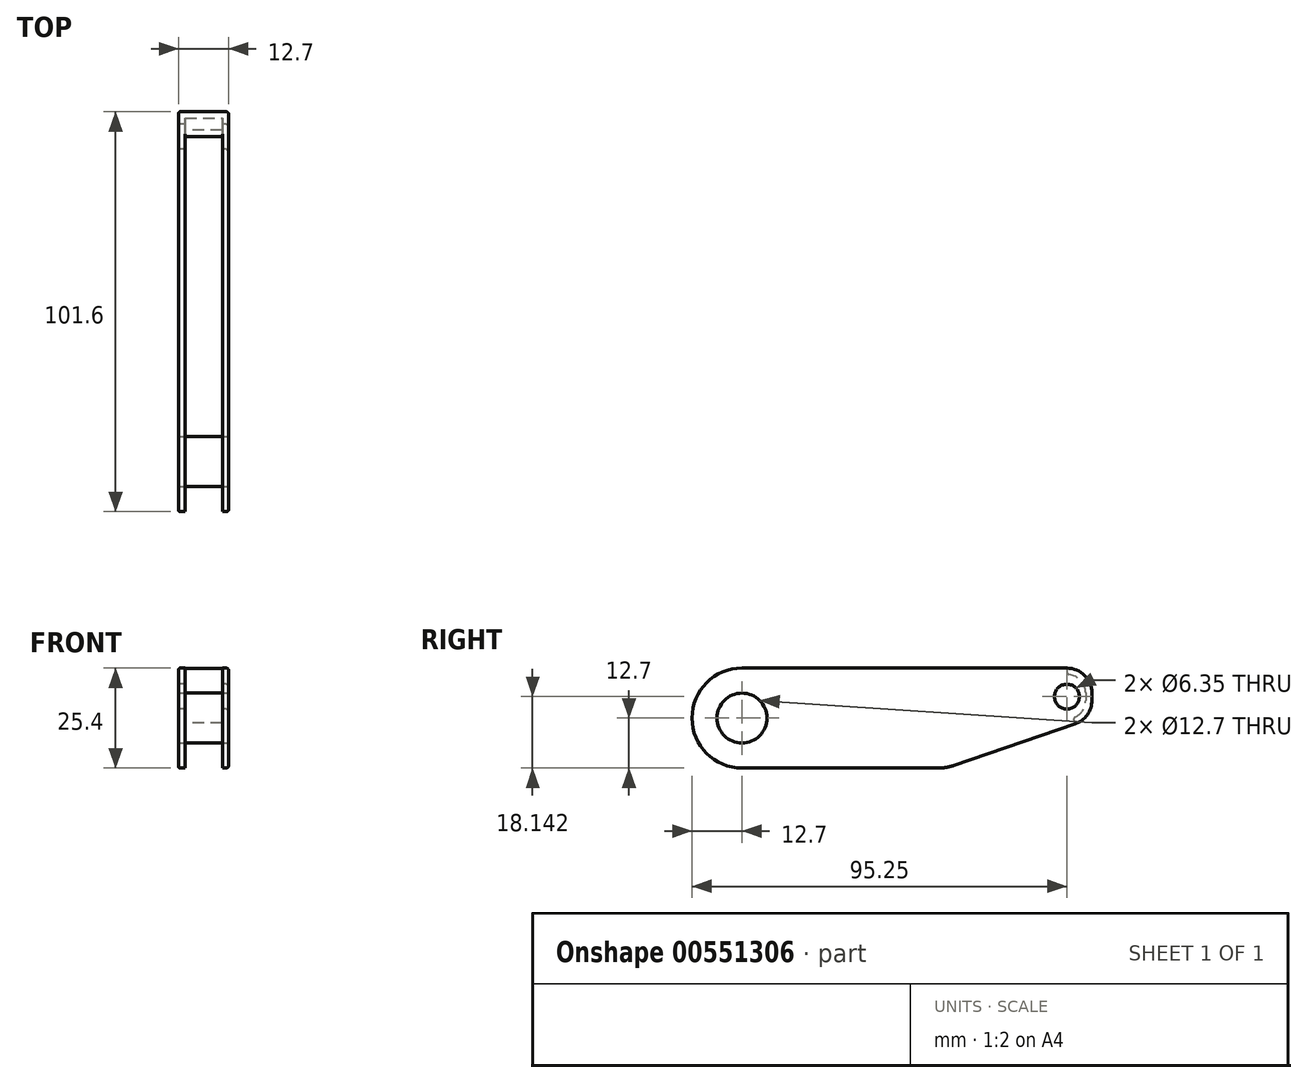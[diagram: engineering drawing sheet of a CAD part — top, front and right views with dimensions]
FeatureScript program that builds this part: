
annotation { "Feature Type Name" : "Feature", "Feature Type Description" : "" }
export const myFeature = defineFeature(function(context is Context, id is Id, definition is map)
    precondition{}
    {
        {
            var Q0;
            Q0=qCreatedBy(makeId("Right.planeOp"),FACE);
            var sketch = newSketch(context, id + "F0", { "sketchPlane" : qUnion([Q0])});
            skLineSegment(sketch, "E0.right", {"start": v(-50.8, 0) * mm, "end": v(-50.8, 0) * mm});
            skPoint(sketch, "E0.middle", {"position": v(0, 0) * mm});
            skArc(sketch, "E1.filletArc", {"start": v(-50.8, 0) * mm, "mid": v(-47.08, -8.98) * mm, "end": v(-38.1, -12.7) * mm});
            skArc(sketch, "E2.filletArc", {"start": v(-38.1, 12.7) * mm, "mid": v(-47.08, 8.98) * mm, "end": v(-50.8, 0) * mm});
            skLineSegment(sketch, "E3.MirrorCS", {"start": v(11.67, -12.7) * mm, "end": v(-38.1, -12.7) * mm});
            skArc(sketch, "E4.MirrorCS", {"start": v(15.8, -12.01) * mm, "mid": v(13.76, -12.53) * mm, "end": v(11.67, -12.7) * mm});
            skLineSegment(sketch, "E5.MirrorCS", {"start": v(15.8, -12.01) * mm, "end": v(46.51, -1.47) * mm});
            skArc(sketch, "E6.MirrorCS", {"start": v(50.8, 4.53) * mm, "mid": v(49.62, 0.84) * mm, "end": v(46.51, -1.47) * mm});
            skLineSegment(sketch, "E7.MirrorCS", {"start": v(50.8, 6.35) * mm, "end": v(50.8, 4.53) * mm});
            skArc(sketch, "E8.MirrorCS", {"start": v(44.45, 12.7) * mm, "mid": v(48.94, 10.84) * mm, "end": v(50.8, 6.35) * mm});
            skLineSegment(sketch, "E9", {"start": v(-38.1, 12.7) * mm, "end": v(44.45, 12.7) * mm});
            skPoint(sketch, "E10", {"position": v(-50.8, 0) * mm});
            skLineSegment(sketch, "E11", {"start": v(-38.1, 12.7) * mm, "end": v(-38.1, -12.7) * mm, "construction": true});
            skLineSegment(sketch, "E12", {"start": v(-38.1, 0) * mm, "end": v(-50.8, 0) * mm, "construction": true});
            skSolve(sketch);
        }
        {
            var Q0;
            Q0=makeQuery(id+"F0.imprint","IMPRINT",FACE,{"disambiguationData":[TD([[makeQuery(id+"F0.imprint","IMPRINT",EDGE,{"derivedFrom":sQuery(id+"F0.wireOp",EDGE,"E1.filletArc")}),1.0]])]});
            extrude(context, id + "F1", {"entities" : qUnion([Q0]), "depth" : 12.7 * mm, "offsetDistance" : 25.4 * mm, "symmetric" : true});
        }
        {
            var Q0;
            Q0=makeQuery(id+"F1.opExtrude","SWEPT_FACE",FACE,{"disambiguationData":[OSD([sQuery(id+"F0.wireOp",EDGE,"E1.filletArc"),sQuery(id+"F0.wireOp",EDGE,"E2.filletArc")])]});
            var Q1;
            Q1=makeQuery(id+"F1.opExtrude","SWEPT_FACE",FACE,{"disambiguationData":[OSD([sQuery(id+"F0.wireOp",EDGE,"E9")])]});
            var Q2;
            Q2=makeQuery(id+"F1.opExtrude","SWEPT_FACE",FACE,{"disambiguationData":[OSD([sQuery(id+"F0.wireOp",EDGE,"E3.MirrorCS")])]});
            var Q3;
            Q3=makeQuery(id+"F1.opExtrude","SWEPT_FACE",FACE,{"disambiguationData":[OSD([sQuery(id+"F0.wireOp",EDGE,"E4.MirrorCS")])]});
            var Q4;
            Q4=makeQuery(id+"F1.opExtrude","SWEPT_FACE",FACE,{"disambiguationData":[OSD([sQuery(id+"F0.wireOp",EDGE,"E5.MirrorCS")])]});
            shell(context, id + "F2", {"entities" : qUnion([Q0, Q1, Q2, Q3, Q4]), "thickness" : 1.59 * mm});
        }
        {
            var Q0;
            Q0=makeQuery(id+"F1.opExtrude","CAP_FACE",FACE,{"disambiguationData":[OSD([sQuery(id+"F0.wireOp",EDGE,"E0.bottom"),sQuery(id+"F0.wireOp",EDGE,"E0.top"),sQuery(id+"F0.wireOp",EDGE,"E0.left"),sQuery(id+"F0.wireOp",EDGE,"N7FiEAlc-xddo-7s0B-UGo9-fPRLMoNNrzdV"),sQuery(id+"F0.wireOp",EDGE,"69d8eef1-d747-4063-9b75-89a39f7d18ea.filletArc"),sQuery(id+"F0.wireOp",EDGE,"d7d453d0-6e9b-41b2-acf9-0c7b81ddef23.filletArc"),sQuery(id+"F0.wireOp",EDGE,"2d4aaca9-d42f-496c-9006-5a42eb52c0ef.filletArc"),sQuery(id+"F0.wireOp",EDGE,"E1.filletArc"),sQuery(id+"F0.wireOp",EDGE,"E2.filletArc")])],"isStart":true});
            var sketch = newSketch(context, id + "F3", { "sketchPlane" : qUnion([Q0])});
            skCircle(sketch, "E13", {"center": v(-44.45, 5.44) * mm, "radius": 3.18 * mm});
            skLineSegment(sketch, "E14.0.0", {"start": v(-44.45, 12.7) * mm, "end": v(38.1, 12.7) * mm});
            skArc(sketch, "E14.0.1", {"start": v(38.1, 12.7) * mm, "mid": v(50.8, 0) * mm, "end": v(38.1, -12.7) * mm});
            skLineSegment(sketch, "E14.0.2", {"start": v(38.1, -12.7) * mm, "end": v(-11.67, -12.7) * mm});
            skArc(sketch, "E14.0.3", {"start": v(-11.67, -12.7) * mm, "mid": v(-13.76, -12.53) * mm, "end": v(-15.8, -12.01) * mm});
            skLineSegment(sketch, "E14.0.4", {"start": v(-15.8, -12.01) * mm, "end": v(-46.51, -1.47) * mm});
            skArc(sketch, "E14.0.5", {"start": v(-46.51, -1.47) * mm, "mid": v(-49.62, 0.84) * mm, "end": v(-50.8, 4.53) * mm});
            skLineSegment(sketch, "E14.0.6", {"start": v(-50.8, 4.53) * mm, "end": v(-50.8, 6.35) * mm});
            skArc(sketch, "E14.0.7", {"start": v(-50.8, 6.35) * mm, "mid": v(-48.94, 10.84) * mm, "end": v(-44.45, 12.7) * mm});
            skLineSegment(sketch, "E15", {"start": v(-44.45, 6.35) * mm, "end": v(-44.45, 4.53) * mm});
            skSolve(sketch);
        }
        {
            var Q0;
            Q0=makeQuery(id+"F3.imprint","IMPRINT",FACE,{"disambiguationData":[TD([[makeQuery(id+"F3.imprint","IMPRINT",EDGE,{"derivedFrom":sQuery(id+"F3.wireOp",EDGE,"E13")}),1.0]])]});
            extrude(context, id + "F4", {"entities" : qUnion([Q0]), "operationType" : NewBodyOperationType.REMOVE, "oppositeDirection" : true, "depth" : 25.4 * mm, "offsetDistance" : 25.4 * mm});
        }
        {
            var Q0;
            Q0=makeQuery(id+"F4.boolean.opBoolean","COPY",EDGE,{"derivedFrom":makeQuery(id+"F4.opExtrude","CAP_EDGE",EDGE,{"disambiguationData":[OSD([sQuery(id+"F3.wireOp",EDGE,"E13")])],"isStart":true})});
            var Q1;
            Q1=makeQuery(id+"F4.boolean.opBoolean","INTERSECT",EDGE,{"derivedFrom":[makeQuery(id+"F1.opExtrude","CAP_FACE",FACE,{"disambiguationData":[OSD([sQuery(id+"F0.wireOp",EDGE,"E0.bottom"),sQuery(id+"F0.wireOp",EDGE,"E0.top"),sQuery(id+"F0.wireOp",EDGE,"E0.left"),sQuery(id+"F0.wireOp",EDGE,"N7FiEAlc-xddo-7s0B-UGo9-fPRLMoNNrzdV"),sQuery(id+"F0.wireOp",EDGE,"69d8eef1-d747-4063-9b75-89a39f7d18ea.filletArc"),sQuery(id+"F0.wireOp",EDGE,"d7d453d0-6e9b-41b2-acf9-0c7b81ddef23.filletArc"),sQuery(id+"F0.wireOp",EDGE,"2d4aaca9-d42f-496c-9006-5a42eb52c0ef.filletArc"),sQuery(id+"F0.wireOp",EDGE,"E1.filletArc"),sQuery(id+"F0.wireOp",EDGE,"E2.filletArc")])],"isStart":false}),makeQuery(id+"F4.opExtrude","SWEPT_FACE",FACE,{"disambiguationData":[OSD([sQuery(id+"F3.wireOp",EDGE,"E13")])]})]});
            fillet(context, id + "F5", {"entities" : qUnion([Q0, Q1]), "radius" : 0.64 * mm, "tangentPropagation" : true, "allowEdgeOverflow" : false});
        }
        {
            var Q0;
            Q0=makeQuery(id+"F1.opExtrude","CAP_FACE",FACE,{"disambiguationData":[OSD([sQuery(id+"F0.wireOp",EDGE,"E0.bottom"),sQuery(id+"F0.wireOp",EDGE,"E0.top"),sQuery(id+"F0.wireOp",EDGE,"E0.left"),sQuery(id+"F0.wireOp",EDGE,"N7FiEAlc-xddo-7s0B-UGo9-fPRLMoNNrzdV"),sQuery(id+"F0.wireOp",EDGE,"69d8eef1-d747-4063-9b75-89a39f7d18ea.filletArc"),sQuery(id+"F0.wireOp",EDGE,"d7d453d0-6e9b-41b2-acf9-0c7b81ddef23.filletArc"),sQuery(id+"F0.wireOp",EDGE,"2d4aaca9-d42f-496c-9006-5a42eb52c0ef.filletArc"),sQuery(id+"F0.wireOp",EDGE,"E1.filletArc"),sQuery(id+"F0.wireOp",EDGE,"E2.filletArc")])],"isStart":true});
            fillet(context, id + "F6", {"entities" : qUnion([Q0]), "radius" : 0.38 * mm, "tangentPropagation" : true, "allowEdgeOverflow" : false});
        }
        {
            var Q0;
            Q0=makeQuery(id+"F1.opExtrude","CAP_FACE",FACE,{"disambiguationData":[OSD([sQuery(id+"F0.wireOp",EDGE,"E0.bottom"),sQuery(id+"F0.wireOp",EDGE,"E0.top"),sQuery(id+"F0.wireOp",EDGE,"E0.left"),sQuery(id+"F0.wireOp",EDGE,"N7FiEAlc-xddo-7s0B-UGo9-fPRLMoNNrzdV"),sQuery(id+"F0.wireOp",EDGE,"69d8eef1-d747-4063-9b75-89a39f7d18ea.filletArc"),sQuery(id+"F0.wireOp",EDGE,"d7d453d0-6e9b-41b2-acf9-0c7b81ddef23.filletArc"),sQuery(id+"F0.wireOp",EDGE,"2d4aaca9-d42f-496c-9006-5a42eb52c0ef.filletArc"),sQuery(id+"F0.wireOp",EDGE,"E1.filletArc"),sQuery(id+"F0.wireOp",EDGE,"E2.filletArc")])],"isStart":false});
            var Q1;
            Q1=makeQuery(id+"F2.opShell","OFFSET_EDGE",EDGE,{"disambiguationData":[OSD([sQuery(id+"F0.wireOp",EDGE,"E8.MirrorCS"),sQuery(id+"F0.wireOp",EDGE,"E9")]),OD(1.0)]});
            var Q2;
            Q2=makeQuery(id+"F2.opShell","OFFSET_EDGE",EDGE,{"disambiguationData":[OSD([sQuery(id+"F0.wireOp",EDGE,"E8.MirrorCS"),sQuery(id+"F0.wireOp",EDGE,"E9")]),OD(2.0)]});
            var Q3;
            Q3=makeQuery(id+"F2.opShell","OFFSET_EDGE",EDGE,{"disambiguationData":[OSD([sQuery(id+"F0.wireOp",EDGE,"E5.MirrorCS"),sQuery(id+"F0.wireOp",EDGE,"E6.MirrorCS")]),OD(1.0)]});
            var Q4;
            Q4=makeQuery(id+"F2.opShell","OFFSET_EDGE",EDGE,{"disambiguationData":[OSD([sQuery(id+"F0.wireOp",EDGE,"E5.MirrorCS"),sQuery(id+"F0.wireOp",EDGE,"E6.MirrorCS")]),OD(2.0)]});
            fillet(context, id + "F7", {"entities" : qUnion([Q0, Q1, Q2, Q3, Q4]), "radius" : 0.64 * mm, "tangentPropagation" : true, "allowEdgeOverflow" : false});
        }
        {
            var Q0;
            Q0=makeQuery(id+"F1.opExtrude","CAP_FACE",FACE,{"disambiguationData":[OSD([sQuery(id+"F0.wireOp",EDGE,"E1.filletArc"),sQuery(id+"F0.wireOp",EDGE,"E2.filletArc"),sQuery(id+"F0.wireOp",EDGE,"E3.MirrorCS"),sQuery(id+"F0.wireOp",EDGE,"E4.MirrorCS"),sQuery(id+"F0.wireOp",EDGE,"E5.MirrorCS"),sQuery(id+"F0.wireOp",EDGE,"E6.MirrorCS"),sQuery(id+"F0.wireOp",EDGE,"E7.MirrorCS"),sQuery(id+"F0.wireOp",EDGE,"E8.MirrorCS"),sQuery(id+"F0.wireOp",EDGE,"E9")])],"isStart":false});
            var sketch = newSketch(context, id + "F8", { "sketchPlane" : qUnion([Q0])});
            skLineSegment(sketch, "E16", {"start": v(-38.1, 12.06) * mm, "end": v(-38.1, -12.07) * mm});
            skCircle(sketch, "E17", {"center": v(-38.1, 0) * mm, "radius": 6.35 * mm});
            skSolve(sketch);
        }
        {
            var Q0;
            Q0 = qSketchRegion(id + "F8", true);
            extrude(context, id + "F9", {"entities" : qUnion([Q0]), "operationType" : NewBodyOperationType.REMOVE, "oppositeDirection" : true, "depth" : 25.4 * mm, "offsetDistance" : 25.4 * mm});
        }
        {
            var Q0;
            Q0=makeQuery(id+"F1.opExtrude","CAP_FACE",FACE,{"disambiguationData":[OSD([sQuery(id+"F0.wireOp",EDGE,"E1.filletArc"),sQuery(id+"F0.wireOp",EDGE,"E2.filletArc"),sQuery(id+"F0.wireOp",EDGE,"E3.MirrorCS"),sQuery(id+"F0.wireOp",EDGE,"E4.MirrorCS"),sQuery(id+"F0.wireOp",EDGE,"E5.MirrorCS"),sQuery(id+"F0.wireOp",EDGE,"E6.MirrorCS"),sQuery(id+"F0.wireOp",EDGE,"E7.MirrorCS"),sQuery(id+"F0.wireOp",EDGE,"E8.MirrorCS"),sQuery(id+"F0.wireOp",EDGE,"E9")])],"isStart":false});
            var sketch = newSketch(context, id + "F10", { "sketchPlane" : qUnion([Q0])});
            skCircle(sketch, "E18", {"center": v(-38.1, 0) * mm, "radius": 6.35 * mm});
            skSolve(sketch);
        }
        {
            var Q0;
            Q0 = qSketchRegion(id + "F10", true);
            extrude(context, id + "F11", {"entities" : qUnion([Q0]), "oppositeDirection" : true, "depth" : 12.7 * mm, "offsetDistance" : 25.4 * mm});
        }
    });
